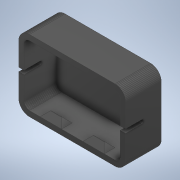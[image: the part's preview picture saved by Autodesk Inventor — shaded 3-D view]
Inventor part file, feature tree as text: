
AUTODESK INVENTOR PART (.ipt)
format: ipt  version: 2020 (Build 240168000, 168)  size: 275,968 bytes
history: native  units: in
note: dims shown in document units (in); Inventor stores cm internally (conversion verified against a paired STEP export)
features: other x3, extrude x2, sketch x2, direct_edit x1
ambient origin geometry x8: Origin, YZ Plane, XZ Plane, XY Plane, X Axis, Y Axis, Z Axis, Center Point
bodies: Solid1 (feature_tree)
feature tree (8):
  other  "ParametricSnapCaseAdaLikeBox-small-ZM20210904"
  other  "MeshFeature1"
  direct_edit  "Direct Edit1"
  extrude  "Extrusion1"  Depth=0.3937in
  extrude  "Extrusion3"  Depth=0.1102in
  sketch  "Sketch1"  dims[d0=0.0394in d1=0.3937in d2=0.3937in d3=0.0984in]
  sketch  "Sketch3"  dims[d4=0.0in d5=0.0in d9=0.1102in d10=0.0in d11=0.0in]
  other  "Scale1"
